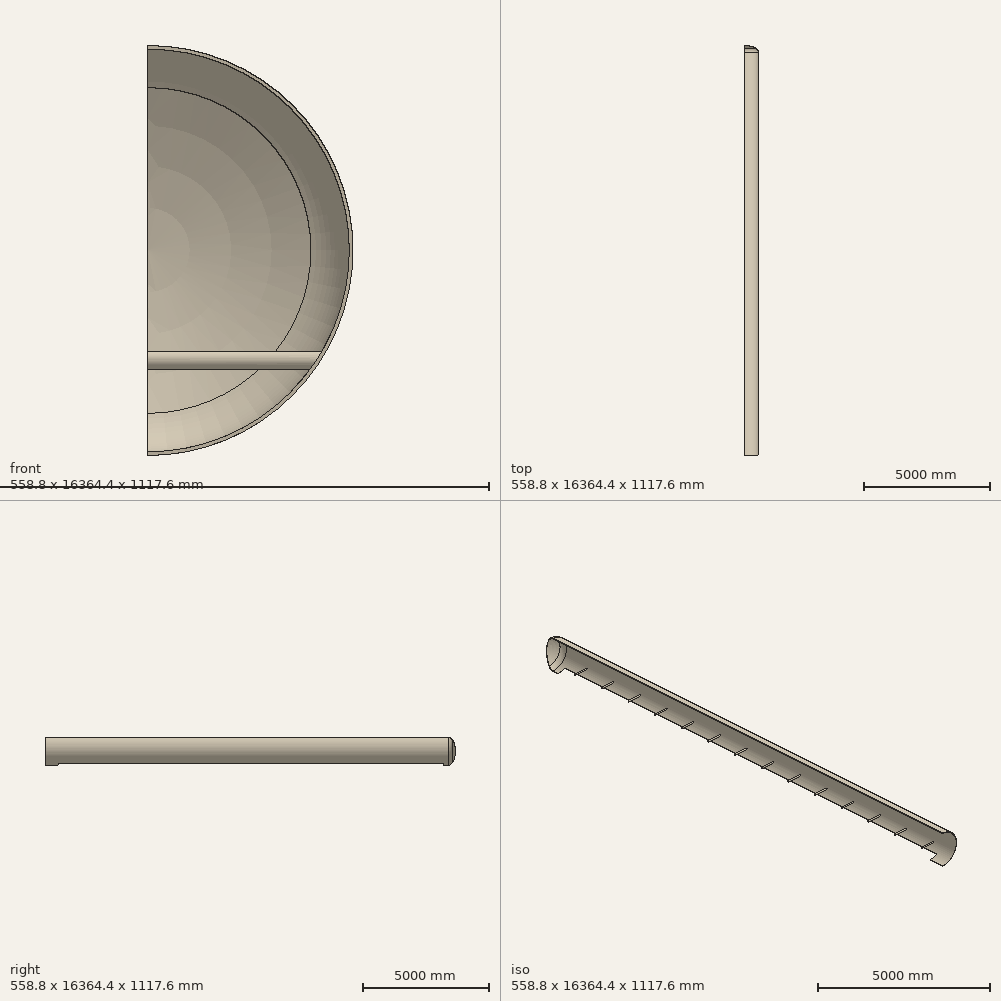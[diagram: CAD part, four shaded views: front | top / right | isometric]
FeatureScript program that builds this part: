
annotation { "Feature Type Name" : "Feature", "Feature Type Description" : "" }
export const myFeature = defineFeature(function(context is Context, id is Id, definition is map)
    precondition{}
    {
        {
            var Q0;
            Q0=qCreatedBy(makeId("Front.planeOp"),FACE);
            var sketch = newSketch(context, id + "F0", { "sketchPlane" : qUnion([Q0])});
            skArc(sketch, "E0", {"start": v(0, -558.8) * mm, "mid": v(558.8, 0) * mm, "end": v(0, 558.8) * mm});
            skLineSegment(sketch, "E1", {"start": v(0, 558.8) * mm, "end": v(0, -558.8) * mm});
            skSolve(sketch);
        }
        {
            var Q0;
            Q0=makeQuery(id+"F0.imprint","IMPRINT",FACE,{"disambiguationData":[TD([[makeQuery(id+"F0.imprint","IMPRINT",EDGE,{"derivedFrom":sQuery(id+"F0.wireOp",EDGE,"HhcUD6RR-tbyw-ofoT-8mBV-F4GgbdSdINna")}),1.0]])]});
            var Q1;
            Q1 = qSketchRegion(id + "F0", true);
            extrude(context, id + "F1", {"entities" : qUnion([Q0, Q1]), "oppositeDirection" : true, "depth" : 16050 * mm});
        }
        {
            var Q0;
            Q0=makeQuery(id+"F1.opExtrude","CAP_FACE",FACE,{"disambiguationData":[OSD([sQuery(id+"F0.wireOp",EDGE,"E0")])],"isStart":true});
            var Q1;
            Q1=makeQuery(id+"F1.opExtrude","CAP_FACE",FACE,{"disambiguationData":[OSD([sQuery(id+"F0.wireOp",EDGE,"E0")])],"isStart":false});
            var Q2;
            Q2=makeQuery(id+"F1.opExtrude","SWEPT_FACE",FACE,{"disambiguationData":[OSD([sQuery(id+"F0.wireOp",EDGE,"E1")])]});
            shell(context, id + "F2", {"entities" : qUnion([Q0, Q1, Q2]), "thickness" : 10 * mm});
        }
        {
            var Q0;
            Q0=qCreatedBy(makeId("Right.planeOp"),FACE);
            var sketch = newSketch(context, id + "F3", { "sketchPlane" : qUnion([Q0])});
            skLineSegment(sketch, "E2", {"start": v(2873.91, 0) * mm, "end": v(3118.36, 0) * mm, "construction": true});
            skLineSegment(sketch, "E3", {"start": v(16050, 548.8) * mm, "end": v(16080, 548.8) * mm});
            skArc(sketch, "E4", {"start": v(16080, 548.8) * mm, "mid": v(16179.65, 520.5) * mm, "end": v(16249.54, 444.02) * mm});
            skArc(sketch, "E5", {"start": v(16249.54, 444.02) * mm, "mid": v(16327.81, 228.11) * mm, "end": v(16354.37, 0) * mm});
            skArc(sketch, "E6.0", {"start": v(16258.49, 448.5) * mm, "mid": v(16337.54, 230.41) * mm, "end": v(16364.37, 0) * mm});
            skArc(sketch, "E6.1", {"start": v(16080, 558.8) * mm, "mid": v(16184.91, 529) * mm, "end": v(16258.49, 448.5) * mm});
            skLineSegment(sketch, "E6.2", {"start": v(16050, 558.8) * mm, "end": v(16080, 558.8) * mm});
            skLineSegment(sketch, "E7", {"start": v(16050, 548.8) * mm, "end": v(16050, 558.8) * mm});
            skLineSegment(sketch, "E8", {"start": v(16354.37, 0) * mm, "end": v(16364.37, 0) * mm});
            skSolve(sketch);
        }
        {
            var Q0;
            Q0 = qSketchRegion(id + "F3", true);
            var Q1;
            Q1=sQuery(id+"F3.wireOp",EDGE,"E6.1");
            var Q2;
            Q2=sQuery(id+"F3.wireOp",EDGE,"E6.0");
            var Q3;
            Q3=sQuery(id+"F3.wireOp",EDGE,"E6.2");
            var Q4;
            Q4=sQuery(id+"F3.wireOp",EDGE,"E3");
            var Q5;
            Q5=sQuery(id+"F3.wireOp",EDGE,"E4");
            var Q6;
            Q6=sQuery(id+"F3.wireOp",EDGE,"E5");
            var Q7;
            Q7=sQuery(id+"F3.wireOp",EDGE,"E7");
            var Q8;
            Q8=sQuery(id+"F3.wireOp",EDGE,"E2");
            revolve(context, id + "F4", {"operationType" : NewBodyOperationType.ADD, "entities" : qUnion([Q0]), "surfaceEntities" : qUnion([Q1, Q2, Q3, Q4, Q5, Q6, Q7]), "axis" : qUnion([Q8]), "revolveType" : RevolveType.ONE_DIRECTION, "angle" : 180 * degree});
        }
        {
            var Q0;
            Q0=makeQuery(id+"F1.opExtrude","CAP_FACE",FACE,{"disambiguationData":[OSD([sQuery(id+"F0.wireOp",EDGE,"E0"),sQuery(id+"F0.wireOp",EDGE,"E1")])],"isStart":true});
            cPlane(context, id + "F5", {"entities" : qUnion([Q0]), "cplaneType" : CPlaneType.OFFSET, "offset" : 520 * mm, "oppositeDirection" : true, "width" : 150 * mm, "height" : 150 * mm});
        }
        {
            var Q0;
            Q0=qCreatedBy(id+"F5.planeOp",FACE);
            var sketch = newSketch(context, id + "F6", { "sketchPlane" : qUnion([Q0])});
            skLineSegment(sketch, "E9", {"start": v(0, 6.36) * mm, "end": v(0, -658.8) * mm});
            skLineSegment(sketch, "E10", {"start": v(0, -658.8) * mm, "end": v(110.6, -658.8) * mm});
            skLineSegment(sketch, "E11", {"start": v(110.6, -658.8) * mm, "end": v(120.6, -676.12) * mm});
            skLineSegment(sketch, "E12", {"start": v(120.6, -676.12) * mm, "end": v(325.67, -557.72) * mm});
            skLineSegment(sketch, "E13", {"start": v(325.67, -557.72) * mm, "end": v(0, 6.36) * mm});
            skSolve(sketch);
        }
        {
            var Q0;
            Q0 = qSketchRegion(id + "F6", true);
            extrude(context, id + "F7", {"entities" : qUnion([Q0]), "operationType" : NewBodyOperationType.REMOVE, "oppositeDirection" : true, "depth" : 15360 * mm});
        }
        {
            var Q0;
            Q0=qCreatedBy(makeId("Right.planeOp"),FACE);
            var sketch = newSketch(context, id + "F8", { "sketchPlane" : qUnion([Q0])});
            skLineSegment(sketch, "E14", {"start": v(0, -300) * mm, "end": v(15174.5, -300) * mm, "construction": true});
            skCircle(sketch, "E15", {"center": v(874.5, -300) * mm, "radius": 25.4 * mm});
            skCircle(sketch, "E16.1.0.0", {"center": v(1974.5, -300) * mm, "radius": 25.4 * mm});
            skCircle(sketch, "E16.2.0.0", {"center": v(3074.5, -300) * mm, "radius": 25.4 * mm});
            skCircle(sketch, "E16.3.0.0", {"center": v(4174.5, -300) * mm, "radius": 25.4 * mm});
            skCircle(sketch, "E16.4.0.0", {"center": v(5274.5, -300) * mm, "radius": 25.4 * mm});
            skCircle(sketch, "E16.5.0.0", {"center": v(6374.5, -300) * mm, "radius": 25.4 * mm});
            skCircle(sketch, "E16.6.0.0", {"center": v(7474.5, -300) * mm, "radius": 25.4 * mm});
            skCircle(sketch, "E16.7.0.0", {"center": v(8574.5, -300) * mm, "radius": 25.4 * mm});
            skCircle(sketch, "E16.8.0.0", {"center": v(9674.5, -300) * mm, "radius": 25.4 * mm});
            skCircle(sketch, "E16.9.0.0", {"center": v(10774.5, -300) * mm, "radius": 25.4 * mm});
            skCircle(sketch, "E16.10.0.0", {"center": v(11874.5, -300) * mm, "radius": 25.4 * mm});
            skCircle(sketch, "E16.11.0.0", {"center": v(12974.5, -300) * mm, "radius": 25.4 * mm});
            skCircle(sketch, "E16.12.0.0", {"center": v(14074.5, -300) * mm, "radius": 25.4 * mm});
            skCircle(sketch, "E16.13.0.0", {"center": v(15174.5, -300) * mm, "radius": 25.4 * mm});
            skLineSegment(sketch, "E16.direction1", {"start": v(874.5, -300) * mm, "end": v(1974.5, -300) * mm, "construction": true});
            skCircle(sketch, "E17", {"center": v(15174.5, -300) * mm, "radius": 22.8 * mm});
            skCircle(sketch, "E18.1.0.0", {"center": v(14074.5, -300) * mm, "radius": 22.8 * mm});
            skCircle(sketch, "E18.2.0.0", {"center": v(12974.5, -300) * mm, "radius": 22.8 * mm});
            skCircle(sketch, "E18.3.0.0", {"center": v(11874.5, -300) * mm, "radius": 22.8 * mm});
            skCircle(sketch, "E18.4.0.0", {"center": v(10774.5, -300) * mm, "radius": 22.8 * mm});
            skCircle(sketch, "E18.5.0.0", {"center": v(9674.5, -300) * mm, "radius": 22.8 * mm});
            skCircle(sketch, "E18.6.0.0", {"center": v(8574.5, -300) * mm, "radius": 22.8 * mm});
            skCircle(sketch, "E18.7.0.0", {"center": v(7474.5, -300) * mm, "radius": 22.8 * mm});
            skCircle(sketch, "E18.8.0.0", {"center": v(6374.5, -300) * mm, "radius": 22.8 * mm});
            skCircle(sketch, "E18.9.0.0", {"center": v(5274.5, -300) * mm, "radius": 22.8 * mm});
            skCircle(sketch, "E18.10.0.0", {"center": v(4174.5, -300) * mm, "radius": 22.8 * mm});
            skCircle(sketch, "E18.11.0.0", {"center": v(3074.5, -300) * mm, "radius": 22.8 * mm});
            skCircle(sketch, "E18.12.0.0", {"center": v(1974.5, -300) * mm, "radius": 22.8 * mm});
            skCircle(sketch, "E18.13.0.0", {"center": v(874.5, -300) * mm, "radius": 22.8 * mm});
            skLineSegment(sketch, "E18.direction1", {"start": v(15174.5, -300) * mm, "end": v(14074.5, -300) * mm, "construction": true});
            skSolve(sketch);
        }
        {
            var Q0;
            Q0 = qSketchRegion(id + "F8", true);
            extrude(context, id + "F9", {"entities" : qUnion([Q0]), "operationType" : NewBodyOperationType.ADD, "endBound" : BoundingType.UP_TO_NEXT, "depth" : 25 * mm});
        }
    });
